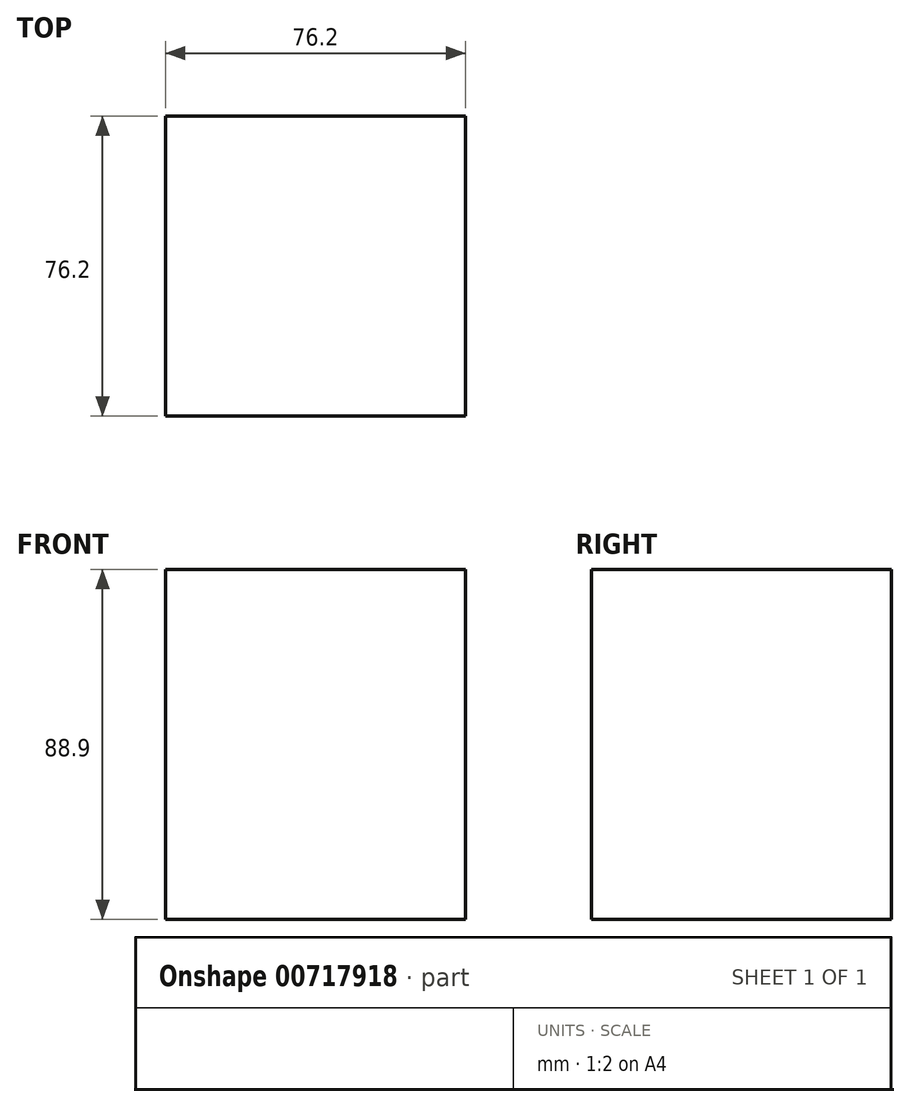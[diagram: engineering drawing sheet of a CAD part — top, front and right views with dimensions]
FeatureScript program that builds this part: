
annotation { "Feature Type Name" : "Feature", "Feature Type Description" : "" }
export const myFeature = defineFeature(function(context is Context, id is Id, definition is map)
    precondition{}
    {
        {
            var Q0;
            Q0=qCreatedBy(makeId("Front.planeOp"),FACE);
            var sketch = newSketch(context, id + "F0", { "sketchPlane" : qUnion([Q0])});
            skLineSegment(sketch, "E0.bottom", {"start": v(-31.47, 36.82) * mm, "end": v(44.73, 36.82) * mm});
            skLineSegment(sketch, "E0.top", {"start": v(-31.47, -39.38) * mm, "end": v(44.73, -39.38) * mm});
            skLineSegment(sketch, "E0.left", {"start": v(-31.47, 36.82) * mm, "end": v(-31.47, -39.38) * mm});
            skLineSegment(sketch, "E0.right", {"start": v(44.73, 36.82) * mm, "end": v(44.73, -39.38) * mm});
            skSolve(sketch);
        }
        {
            var Q0;
            Q0=makeQuery(id+"F0.imprint","IMPRINT",FACE,{"disambiguationData":[TD([[makeQuery(id+"F0.imprint","IMPRINT",EDGE,{"derivedFrom":sQuery(id+"F0.wireOp",EDGE,"E0.bottom")}),-1.0]])]});
            extrude(context, id + "F1", {"entities" : qUnion([Q0]), "endBound" : BoundingType.SYMMETRIC, "depth" : 76.2 * mm, "offsetDistance" : 25.4 * mm});
        }
        {
            var Q0;
            Q0=makeQuery(id+"F1.opExtrude","SWEPT_FACE",FACE,{"disambiguationData":[OSD([sQuery(id+"F0.wireOp",EDGE,"E0.bottom")])]});
            extrude(context, id + "F2", {"entities" : qUnion([Q0]), "operationType" : NewBodyOperationType.ADD, "endBound" : BoundingType.SYMMETRIC, "depth" : 25.4 * mm, "offsetDistance" : 25.4 * mm});
        }
    });
